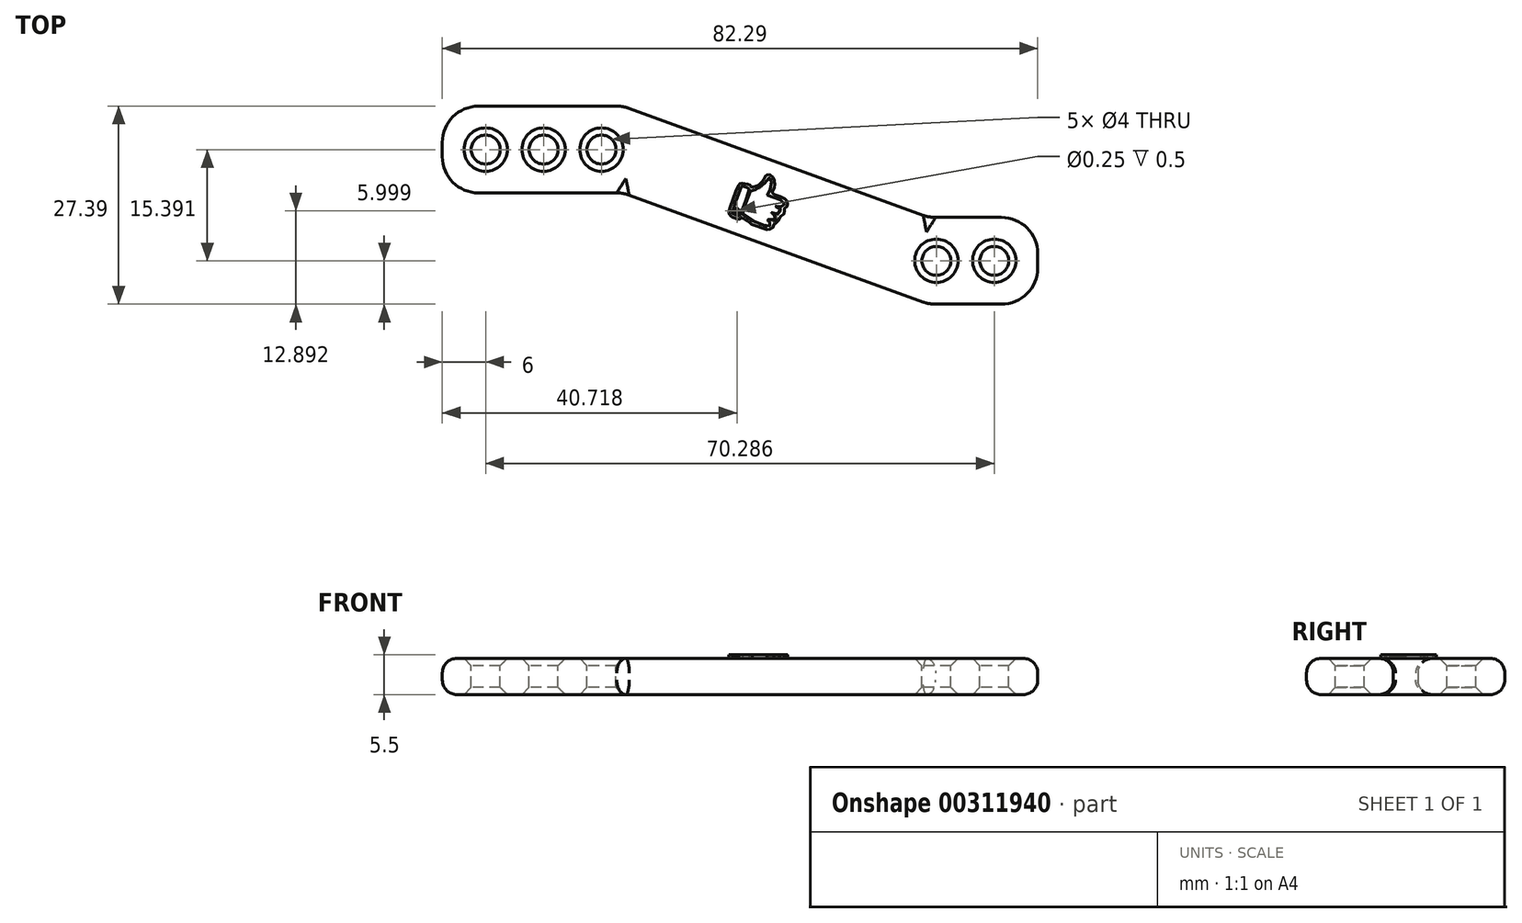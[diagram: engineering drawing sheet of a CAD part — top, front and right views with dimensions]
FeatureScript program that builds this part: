
annotation { "Feature Type Name" : "Feature", "Feature Type Description" : "" }
export const myFeature = defineFeature(function(context is Context, id is Id, definition is map)
    precondition{}
    {
        {
            var Q0;
            Q0=qCreatedBy(makeId("Top.planeOp"),FACE);
            var sketch = newSketch(context, id + "F0", { "sketchPlane" : qUnion([Q0])});
            skLineSegment(sketch, "E0.bottom", {"start": v(0, 12) * mm, "end": v(25, 12) * mm});
            skLineSegment(sketch, "E0.top", {"start": v(0, 0) * mm, "end": v(25, 0) * mm});
            skLineSegment(sketch, "E0.left", {"start": v(0, 12) * mm, "end": v(0, 0) * mm});
            skLineSegment(sketch, "E0.right", {"start": v(25, 12) * mm, "end": v(25, 0) * mm});
            skLineSegment(sketch, "E1.bottom", {"start": v(67.29, -3.4) * mm, "end": v(82.29, -3.4) * mm});
            skLineSegment(sketch, "E1.top", {"start": v(67.29, -15.4) * mm, "end": v(82.29, -15.4) * mm});
            skLineSegment(sketch, "E1.left", {"start": v(67.29, -3.4) * mm, "end": v(67.29, -15.4) * mm});
            skLineSegment(sketch, "E1.right", {"start": v(82.29, -3.4) * mm, "end": v(82.29, -15.4) * mm});
            skLineSegment(sketch, "E2", {"start": v(25, 12) * mm, "end": v(67.29, -3.4) * mm});
            skLineSegment(sketch, "E3", {"start": v(25, 0) * mm, "end": v(67.29, -15.4) * mm});
            skSolve(sketch);
        }
        {
            var Q0;
            Q0=makeQuery(id+"F0.imprint","IMPRINT",FACE,{"disambiguationData":[TD([[makeQuery(id+"F0.imprint","IMPRINT",EDGE,{"derivedFrom":sQuery(id+"F0.wireOp",EDGE,"E0.bottom")}),-1.0]])]});
            var Q1;
            Q1=makeQuery(id+"F0.imprint","IMPRINT",FACE,{"disambiguationData":[TD([[makeQuery(id+"F0.imprint","IMPRINT",EDGE,{"derivedFrom":sQuery(id+"F0.wireOp",EDGE,"E0.right")}),1.0]])]});
            var Q2;
            Q2=makeQuery(id+"F0.imprint","IMPRINT",FACE,{"disambiguationData":[TD([[makeQuery(id+"F0.imprint","IMPRINT",EDGE,{"derivedFrom":sQuery(id+"F0.wireOp",EDGE,"E1.bottom")}),-1.0]])]});
            extrude(context, id + "F1", {"entities" : qUnion([Q0, Q1, Q2]), "depth" : 5 * mm});
        }
        {
            var Q0;
            Q0=makeQuery(id+"F1.opExtrude","CAP_FACE",FACE,{"disambiguationData":[OSD([sQuery(id+"F0.wireOp",EDGE,"E0.bottom"),sQuery(id+"F0.wireOp",EDGE,"E0.top"),sQuery(id+"F0.wireOp",EDGE,"E0.left"),sQuery(id+"F0.wireOp",EDGE,"E1.bottom"),sQuery(id+"F0.wireOp",EDGE,"E1.top"),sQuery(id+"F0.wireOp",EDGE,"E1.right"),sQuery(id+"F0.wireOp",EDGE,"E2"),sQuery(id+"F0.wireOp",EDGE,"E3")])],"isStart":false});
            var sketch = newSketch(context, id + "F2", { "sketchPlane" : qUnion([Q0])});
            skCircle(sketch, "E4", {"center": v(6, 6) * mm, "radius": 2 * mm});
            skCircle(sketch, "E5", {"center": v(76.29, -9.4) * mm, "radius": 2 * mm});
            skCircle(sketch, "E6.1.0.0", {"center": v(14, 6) * mm, "radius": 2 * mm});
            skCircle(sketch, "E6.2.0.0", {"center": v(22, 6) * mm, "radius": 2 * mm});
            skLineSegment(sketch, "E6.direction1", {"start": v(6, 6) * mm, "end": v(14, 6) * mm, "construction": true});
            skCircle(sketch, "E7.1.0.0", {"center": v(68.29, -9.4) * mm, "radius": 2 * mm});
            skLineSegment(sketch, "E7.direction1", {"start": v(76.29, -9.4) * mm, "end": v(68.29, -9.4) * mm, "construction": true});
            skSolve(sketch);
        }
        {
            var Q0;
            Q0=makeQuery(id+"F2.imprint","IMPRINT",FACE,{"disambiguationData":[TD([[makeQuery(id+"F2.imprint","IMPRINT",EDGE,{"derivedFrom":sQuery(id+"F2.wireOp",EDGE,"E4")}),1.0]])]});
            var Q1;
            Q1=makeQuery(id+"F2.imprint","IMPRINT",FACE,{"disambiguationData":[TD([[makeQuery(id+"F2.imprint","IMPRINT",EDGE,{"derivedFrom":sQuery(id+"F2.wireOp",EDGE,"E6.1.0.0")}),1.0]])]});
            var Q2;
            Q2=makeQuery(id+"F2.imprint","IMPRINT",FACE,{"disambiguationData":[TD([[makeQuery(id+"F2.imprint","IMPRINT",EDGE,{"derivedFrom":sQuery(id+"F2.wireOp",EDGE,"E6.2.0.0")}),1.0]])]});
            var Q3;
            Q3=makeQuery(id+"F2.imprint","IMPRINT",FACE,{"disambiguationData":[TD([[makeQuery(id+"F2.imprint","IMPRINT",EDGE,{"derivedFrom":sQuery(id+"F2.wireOp",EDGE,"E7.1.0.0")}),1.0]])]});
            var Q4;
            Q4=makeQuery(id+"F2.imprint","IMPRINT",FACE,{"disambiguationData":[TD([[makeQuery(id+"F2.imprint","IMPRINT",EDGE,{"derivedFrom":sQuery(id+"F2.wireOp",EDGE,"E5")}),1.0]])]});
            extrude(context, id + "F3", {"entities" : qUnion([Q0, Q1, Q2, Q3, Q4]), "operationType" : NewBodyOperationType.REMOVE, "endBound" : BoundingType.THROUGH_ALL, "oppositeDirection" : true, "depth" : 5 * mm});
        }
        {
            var Q0;
            Q0=makeQuery(id+"F1.opExtrude","CAP_EDGE",EDGE,{"disambiguationData":[OSD([sQuery(id+"F0.wireOp",EDGE,"E1.top")])],"isStart":false});
            var Q1;
            Q1=makeQuery(id+"F1.opExtrude","CAP_EDGE",EDGE,{"disambiguationData":[OSD([sQuery(id+"F0.wireOp",EDGE,"E3")])],"isStart":false});
            var Q2;
            Q2=makeQuery(id+"F1.opExtrude","CAP_EDGE",EDGE,{"disambiguationData":[OSD([sQuery(id+"F0.wireOp",EDGE,"E1.right")])],"isStart":false});
            var Q3;
            Q3=makeQuery(id+"F1.opExtrude","CAP_EDGE",EDGE,{"disambiguationData":[OSD([sQuery(id+"F0.wireOp",EDGE,"E1.bottom")])],"isStart":false});
            var Q4;
            Q4=makeQuery(id+"F1.opExtrude","CAP_EDGE",EDGE,{"disambiguationData":[OSD([sQuery(id+"F0.wireOp",EDGE,"E2")])],"isStart":false});
            var Q5;
            Q5=makeQuery(id+"F1.opExtrude","CAP_EDGE",EDGE,{"disambiguationData":[OSD([sQuery(id+"F0.wireOp",EDGE,"E0.left")])],"isStart":false});
            var Q6;
            Q6=makeQuery(id+"F1.opExtrude","CAP_EDGE",EDGE,{"disambiguationData":[OSD([sQuery(id+"F0.wireOp",EDGE,"E0.bottom")])],"isStart":false});
            var Q7;
            Q7=makeQuery(id+"F1.opExtrude","CAP_EDGE",EDGE,{"disambiguationData":[OSD([sQuery(id+"F0.wireOp",EDGE,"E0.top")])],"isStart":false});
            var Q8;
            Q8=makeQuery(id+"F1.opExtrude","CAP_EDGE",EDGE,{"disambiguationData":[OSD([sQuery(id+"F0.wireOp",EDGE,"E3")])],"isStart":true});
            var Q9;
            Q9=makeQuery(id+"F1.opExtrude","CAP_EDGE",EDGE,{"disambiguationData":[OSD([sQuery(id+"F0.wireOp",EDGE,"E0.top")])],"isStart":true});
            var Q10;
            Q10=makeQuery(id+"F1.opExtrude","CAP_EDGE",EDGE,{"disambiguationData":[OSD([sQuery(id+"F0.wireOp",EDGE,"E0.left")])],"isStart":true});
            var Q11;
            Q11=makeQuery(id+"F1.opExtrude","CAP_EDGE",EDGE,{"disambiguationData":[OSD([sQuery(id+"F0.wireOp",EDGE,"E0.bottom")])],"isStart":true});
            var Q12;
            Q12=makeQuery(id+"F1.opExtrude","CAP_EDGE",EDGE,{"disambiguationData":[OSD([sQuery(id+"F0.wireOp",EDGE,"E2")])],"isStart":true});
            var Q13;
            Q13=makeQuery(id+"F1.opExtrude","CAP_EDGE",EDGE,{"disambiguationData":[OSD([sQuery(id+"F0.wireOp",EDGE,"E1.bottom")])],"isStart":true});
            var Q14;
            Q14=makeQuery(id+"F1.opExtrude","CAP_EDGE",EDGE,{"disambiguationData":[OSD([sQuery(id+"F0.wireOp",EDGE,"E1.top")])],"isStart":true});
            var Q15;
            Q15=makeQuery(id+"F1.opExtrude","CAP_EDGE",EDGE,{"disambiguationData":[OSD([sQuery(id+"F0.wireOp",EDGE,"E1.right")])],"isStart":true});
            fillet(context, id + "F4", {"entities" : qUnion([Q0, Q1, Q2, Q3, Q4, Q5, Q6, Q7, Q8, Q9, Q10, Q11, Q12, Q13, Q14, Q15]), "radius" : 2 * mm, "tangentPropagation" : true, "allowEdgeOverflow" : false});
        }
        {
            var Q0;
            Q0=makeQuery(id+"F1.opExtrude","SWEPT_EDGE",EDGE,{"disambiguationData":[OSD([sQuery(id+"F0.wireOp",EDGE,"E0.top"),sQuery(id+"F0.wireOp",EDGE,"E0.left")])]});
            var Q1;
            Q1=makeQuery(id+"F1.opExtrude","SWEPT_EDGE",EDGE,{"disambiguationData":[OSD([sQuery(id+"F0.wireOp",EDGE,"E0.top"),sQuery(id+"F0.wireOp",EDGE,"E0.right"),sQuery(id+"F0.wireOp",EDGE,"E3")])]});
            var Q2;
            Q2=makeQuery(id+"F1.opExtrude","SWEPT_EDGE",EDGE,{"disambiguationData":[OSD([sQuery(id+"F0.wireOp",EDGE,"E0.bottom"),sQuery(id+"F0.wireOp",EDGE,"E0.left")])]});
            var Q3;
            Q3=makeQuery(id+"F1.opExtrude","SWEPT_EDGE",EDGE,{"disambiguationData":[OSD([sQuery(id+"F0.wireOp",EDGE,"E1.top"),sQuery(id+"F0.wireOp",EDGE,"E1.right")])]});
            var Q4;
            Q4=makeQuery(id+"F1.opExtrude","SWEPT_EDGE",EDGE,{"disambiguationData":[OSD([sQuery(id+"F0.wireOp",EDGE,"E1.bottom"),sQuery(id+"F0.wireOp",EDGE,"E1.right")])]});
            var Q5;
            Q5=makeQuery(id+"F1.opExtrude","SWEPT_EDGE",EDGE,{"disambiguationData":[OSD([sQuery(id+"F0.wireOp",EDGE,"E1.top"),sQuery(id+"F0.wireOp",EDGE,"E1.left"),sQuery(id+"F0.wireOp",EDGE,"E3")])]});
            var Q6;
            Q6=makeQuery(id+"F1.opExtrude","SWEPT_EDGE",EDGE,{"disambiguationData":[OSD([sQuery(id+"F0.wireOp",EDGE,"E1.bottom"),sQuery(id+"F0.wireOp",EDGE,"E1.left"),sQuery(id+"F0.wireOp",EDGE,"E2")])]});
            var Q7;
            Q7=makeQuery(id+"F1.opExtrude","SWEPT_EDGE",EDGE,{"disambiguationData":[OSD([sQuery(id+"F0.wireOp",EDGE,"E0.bottom"),sQuery(id+"F0.wireOp",EDGE,"E0.right"),sQuery(id+"F0.wireOp",EDGE,"E2")])]});
            fillet(context, id + "F5", {"entities" : qUnion([Q0, Q1, Q2, Q3, Q4, Q5, Q6, Q7]), "radius" : 5 * mm, "tangentPropagation" : true, "allowEdgeOverflow" : false});
        }
        {
            var Q0;
            Q0=makeQuery(id+"F1.opExtrude","CAP_FACE",FACE,{"disambiguationData":[OSD([sQuery(id+"F0.wireOp",EDGE,"E0.bottom"),sQuery(id+"F0.wireOp",EDGE,"E0.top"),sQuery(id+"F0.wireOp",EDGE,"E0.left"),sQuery(id+"F0.wireOp",EDGE,"E1.bottom"),sQuery(id+"F0.wireOp",EDGE,"E1.top"),sQuery(id+"F0.wireOp",EDGE,"E1.right"),sQuery(id+"F0.wireOp",EDGE,"E2"),sQuery(id+"F0.wireOp",EDGE,"E3")])],"isStart":false});
            var Q1;
            Q1=makeQuery(id+"F1.opExtrude","CAP_FACE",FACE,{"disambiguationData":[OSD([sQuery(id+"F0.wireOp",EDGE,"E0.bottom"),sQuery(id+"F0.wireOp",EDGE,"E0.top"),sQuery(id+"F0.wireOp",EDGE,"E0.left"),sQuery(id+"F0.wireOp",EDGE,"E1.bottom"),sQuery(id+"F0.wireOp",EDGE,"E1.top"),sQuery(id+"F0.wireOp",EDGE,"E1.right"),sQuery(id+"F0.wireOp",EDGE,"E2"),sQuery(id+"F0.wireOp",EDGE,"E3")])],"isStart":true});
            chamfer(context, id + "F6", {"entities" : qUnion([Q0, Q1]), "width" : 1 * mm, "tangentPropagation" : true});
        }
        {
            var Q0;
            Q0=makeQuery(id+"F1.opExtrude","CAP_FACE",FACE,{"disambiguationData":[OSD([sQuery(id+"F0.wireOp",EDGE,"E0.bottom"),sQuery(id+"F0.wireOp",EDGE,"E0.top"),sQuery(id+"F0.wireOp",EDGE,"E0.left"),sQuery(id+"F0.wireOp",EDGE,"E1.bottom"),sQuery(id+"F0.wireOp",EDGE,"E1.top"),sQuery(id+"F0.wireOp",EDGE,"E1.right"),sQuery(id+"F0.wireOp",EDGE,"E2"),sQuery(id+"F0.wireOp",EDGE,"E3")])],"isStart":false});
            var sketch = newSketch(context, id + "F7", { "sketchPlane" : qUnion([Q0])});
            skPoint(sketch, "E8.34.internal.snap0", {"position": v(47.5, -2.19) * mm});
            skPoint(sketch, "E8.47.internal.snap0", {"position": v(45.32, 2.48) * mm});
            skFitSpline(sketch, "E8", {"points": [v(39.6, -2.57) * mm, v(40.89, 0.95) * mm, v(41.17, 1.26) * mm, v(41.53, 1.34) * mm, v(42.14, 1.2) * mm, v(42.55, 1.07) * mm, v(42.73, 0.78) * mm, v(43.02, 0.84) * mm, v(43.21, 0.87) * mm, v(43.76, 1.1) * mm, v(44.14, 1.53) * mm, v(44.43, 1.89) * mm, v(44.57, 2.2) * mm, v(44.69, 2.34) * mm, v(44.86, 2.45) * mm, v(45.14, 2.54) * mm, v(45.32, 2.48) * mm, v(45.6, 2.26) * mm, v(45.76, 2) * mm, v(45.9, 1.6) * mm, v(45.98, 1.22) * mm, v(45.87, 0.74) * mm, v(45.72, 0.32) * mm, v(45.5, 0) * mm, v(45.62, 0) * mm, v(45.78, -0.15) * mm, v(46, -0.24) * mm, v(47.12, -0.69) * mm, v(47.45, -0.87) * mm, v(47.52, -1) * mm, v(47.68, -1.3) * mm, v(47.7, -1.6) * mm, v(47.61, -1.85) * mm, v(47.53, -2.09) * mm, v(47.2, -2.19) * mm, v(47.27, -2.36) * mm, v(47.28, -2.78) * mm, v(47.24, -2.88) * mm, v(46.97, -3.12) * mm, v(46.61, -3.31) * mm, v(46.63, -3.43) * mm, v(46.53, -3.73) * mm, v(46.3, -4.02) * mm, v(46.05, -4.22) * mm, v(45.83, -4.28) * mm, v(45.83, -4.44) * mm, v(45.74, -4.75) * mm, v(45.32, -4.99) * mm, v(45.1, -5.07) * mm, v(44.87, -5.1) * mm, v(43.9, -4.75) * mm, v(42.83, -4.36) * mm, v(42.44, -4.06) * mm, v(42.24, -3.92) * mm, v(41.91, -3.7) * mm, v(41.62, -3.54) * mm, v(41.35, -3.4) * mm, v(41.18, -3.54) * mm, v(40.92, -3.66) * mm, v(40.66, -3.57) * mm, v(40.08, -3.36) * mm, v(39.83, -3.15) * mm, v(39.63, -2.9) * mm, v(39.6, -2.57) * mm]});
            skFitSpline(sketch, "E9", {"points": [v(40.13, -2.84) * mm, v(40.84, -3.15) * mm, v(41, -3.2) * mm, v(41.07, -3.15) * mm, v(41.18, -3.07) * mm, v(42.4, 0.47) * mm, v(42.4, 0.55) * mm, v(42.34, 0.63) * mm, v(42.23, 0.68) * mm, v(41.59, 0.92) * mm, v(41.5, 0.94) * mm, v(41.4, 0.92) * mm, v(41.33, 0.83) * mm, v(40.06, -2.7) * mm, v(40.13, -2.84) * mm]});
            skCircle(sketch, "E10", {"center": v(40.72, -2.5) * mm, "radius": 0.13 * mm});
            skCircle(sketch, "E11", {"center": v(40.72, -2.5) * mm, "radius": 0.34 * mm});
            skFitSpline(sketch, "E12", {"points": [v(41.51, -2.94) * mm, v(41.49, -2.87) * mm, v(41.49, -2.75) * mm, v(41.9, -1.61) * mm, v(42.38, -0.26) * mm, v(42.57, 0.23) * mm, v(42.62, 0.32) * mm, v(42.68, 0.37) * mm, v(42.83, 0.34) * mm, v(43.04, 0.39) * mm, v(43.26, 0.42) * mm, v(43.84, 0.62) * mm, v(44.45, 1.18) * mm, v(44.76, 1.65) * mm, v(44.89, 2) * mm, v(45, 2.07) * mm, v(45.07, 2.07) * mm, v(45.15, 2.05) * mm, v(45.25, 2) * mm, v(45.31, 1.9) * mm, v(45.42, 1.74) * mm, v(45.46, 1.61) * mm, v(45.5, 1.5) * mm, v(45.5, 1.18) * mm, v(45.49, 0.97) * mm, v(45.34, 0.56) * mm, v(45.18, 0.24) * mm, v(45, -0.07) * mm, v(44.86, -0.23) * mm, v(45.08, -0.32) * mm, v(45.52, -0.5) * mm, v(46.87, -1.02) * mm, v(47.04, -1.13) * mm, v(47.2, -1.25) * mm, v(47.25, -1.34) * mm, v(47.26, -1.54) * mm, v(47.23, -1.66) * mm, v(47.17, -1.74) * mm, v(47.1, -1.84) * mm, v(46.99, -1.9) * mm, v(46.93, -1.92) * mm, v(46.74, -1.93) * mm, v(46.52, -1.84) * mm, v(46.2, -1.72) * mm, v(46.13, -1.75) * mm, v(46.1, -1.8) * mm, v(46.1, -1.91) * mm, v(46.26, -1.98) * mm, v(46.49, -2.06) * mm, v(46.65, -2.13) * mm, v(46.78, -2.28) * mm, v(46.8, -2.5) * mm, v(46.7, -2.73) * mm, v(46.5, -2.88) * mm, v(46.28, -2.96) * mm, v(46, -2.86) * mm, v(45.63, -2.74) * mm, v(45.57, -2.7) * mm, v(45.54, -2.74) * mm, v(45.48, -2.78) * mm, v(45.5, -2.86) * mm, v(45.54, -2.93) * mm, v(45.64, -2.95) * mm, v(45.8, -3.02) * mm, v(45.95, -3.08) * mm, v(46.1, -3.16) * mm, v(46.2, -3.27) * mm, v(46.18, -3.5) * mm, v(46.02, -3.72) * mm, v(45.8, -3.92) * mm, v(45.48, -3.89) * mm, v(44.99, -3.7) * mm, v(44.9, -3.72) * mm, v(44.86, -3.8) * mm, v(44.87, -3.88) * mm, v(44.98, -3.94) * mm, v(45.14, -4.01) * mm, v(45.33, -4.07) * mm, v(45.4, -4.18) * mm, v(45.43, -4.3) * mm, v(45.4, -4.38) * mm, v(45.3, -4.49) * mm, v(45.22, -4.59) * mm, v(45.1, -4.63) * mm, v(44.94, -4.63) * mm, v(44.68, -4.58) * mm, v(44.17, -4.37) * mm, v(43.5, -4.11) * mm, v(42.92, -3.84) * mm, v(42.26, -3.44) * mm, v(41.51, -2.94) * mm]});
            skSolve(sketch);
        }
        {
            var Q0;
            Q0=makeQuery(id+"F7.imprint","IMPRINT",FACE,{"disambiguationData":[TD([[makeQuery(id+"F7.imprint","IMPRINT",EDGE,{"derivedFrom":sQuery(id+"F7.wireOp",EDGE,"E10")}),-1.0]])]});
            var Q1;
            Q1=makeQuery(id+"F7.imprint","IMPRINT",FACE,{"disambiguationData":[TD([[makeQuery(id+"F7.imprint","IMPRINT",EDGE,{"derivedFrom":sQuery(id+"F7.wireOp",EDGE,"E9")}),-1.0]])]});
            extrude(context, id + "F8", {"entities" : qUnion([Q0, Q1]), "operationType" : NewBodyOperationType.ADD, "depth" : .5 * mm});
        }
    });
